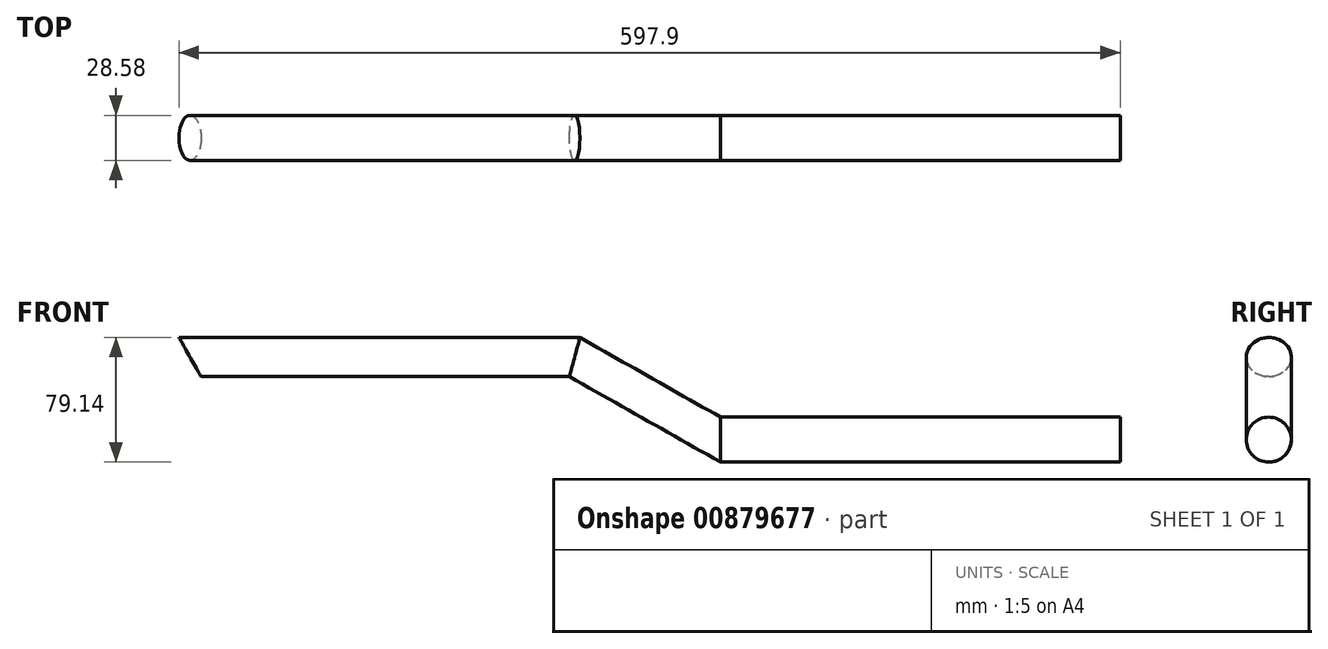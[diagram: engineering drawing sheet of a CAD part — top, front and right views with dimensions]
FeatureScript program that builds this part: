
annotation { "Feature Type Name" : "Feature", "Feature Type Description" : "" }
export const myFeature = defineFeature(function(context is Context, id is Id, definition is map)
    precondition{}
    {
        {
            var Q0;
            Q0=qCreatedBy(makeId("Right.planeOp"),FACE);
            var sketch = newSketch(context, id + "F0", { "sketchPlane" : qUnion([Q0])});
            skCircle(sketch, "E0", {"center": v(0, 0) * mm, "radius": 14.29 * mm});
            skSolve(sketch);
        }
        {
            var Q0;
            Q0=makeQuery(id+"F0.imprint","IMPRINT",FACE,{"disambiguationData":[TD([[makeQuery(id+"F0.imprint","IMPRINT",EDGE,{"derivedFrom":sQuery(id+"F0.wireOp",EDGE,"E0")}),1.0]])]});
            extrude(context, id + "F1", {"entities" : qUnion([Q0]), "depth" : 254 * mm, "offsetDistance" : 25.4 * mm});
        }
        {
            var Q0;
            Q0=qCreatedBy(makeId("Front.planeOp"),FACE);
            var sketch = newSketch(context, id + "F2", { "sketchPlane" : qUnion([Q0])});
            skLineSegment(sketch, "E1", {"start": v(0, 0) * mm, "end": v(-92.56, 52.42) * mm});
            skLineSegment(sketch, "E2", {"start": v(-92.56, 52.42) * mm, "end": v(-336.86, 52.42) * mm});
            skSolve(sketch);
        }
        {
            var Q0;
            Q0=makeQuery(id+"F1.opExtrude","CAP_FACE",FACE,{"disambiguationData":[OSD([sQuery(id+"F0.wireOp",EDGE,"E0")])],"isStart":true});
            var Q1;
            Q1=sQuery(id+"F2.wireOp",EDGE,"E2");
            var Q2;
            Q2=sQuery(id+"F2.wireOp",EDGE,"E1");
            sweep(context, id + "F3", {"operationType" : NewBodyOperationType.ADD, "profiles" : qUnion([Q0]), "path" : qUnion([Q1, Q2])});
        }
    });
